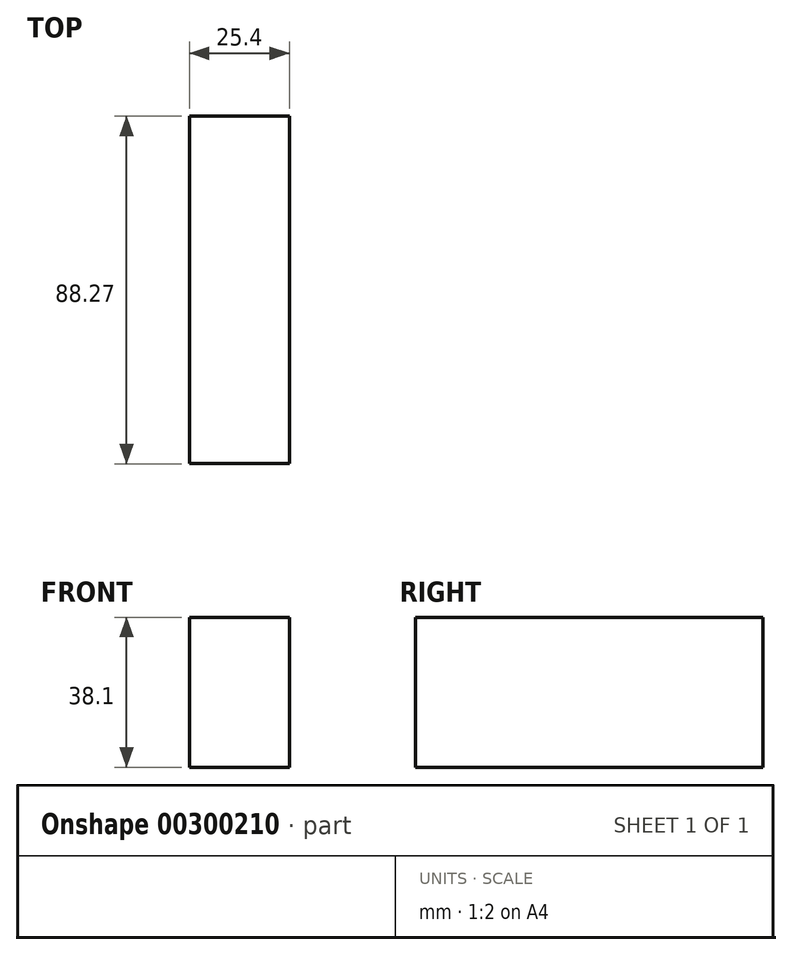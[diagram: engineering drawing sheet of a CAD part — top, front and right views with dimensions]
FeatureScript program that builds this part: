
annotation { "Feature Type Name" : "Feature", "Feature Type Description" : "" }
export const myFeature = defineFeature(function(context is Context, id is Id, definition is map)
    precondition{}
    {
        {
            var Q0;
            Q0=qCreatedBy(makeId("Right.planeOp"),FACE);
            var sketch = newSketch(context, id + "F0", { "sketchPlane" : qUnion([Q0])});
            skLineSegment(sketch, "E0.bottom", {"start": v(107.48, 43.58) * mm, "end": v(19.21, 43.58) * mm});
            skLineSegment(sketch, "E0.top", {"start": v(107.48, 5.48) * mm, "end": v(19.21, 5.48) * mm});
            skLineSegment(sketch, "E0.left", {"start": v(107.48, 43.58) * mm, "end": v(107.48, 5.48) * mm});
            skLineSegment(sketch, "E0.right", {"start": v(19.21, 43.58) * mm, "end": v(19.21, 5.48) * mm});
            skSolve(sketch);
        }
        {
            var Q0;
            Q0=makeQuery(id+"F0.imprint","IMPRINT",FACE,{"disambiguationData":[TD([[makeQuery(id+"F0.imprint","IMPRINT",EDGE,{"derivedFrom":sQuery(id+"F0.wireOp",EDGE,"E0.bottom")}),1.0]])]});
            extrude(context, id + "F1", {"entities" : qUnion([Q0]), "depth" : 25.4 * mm});
        }
    });
